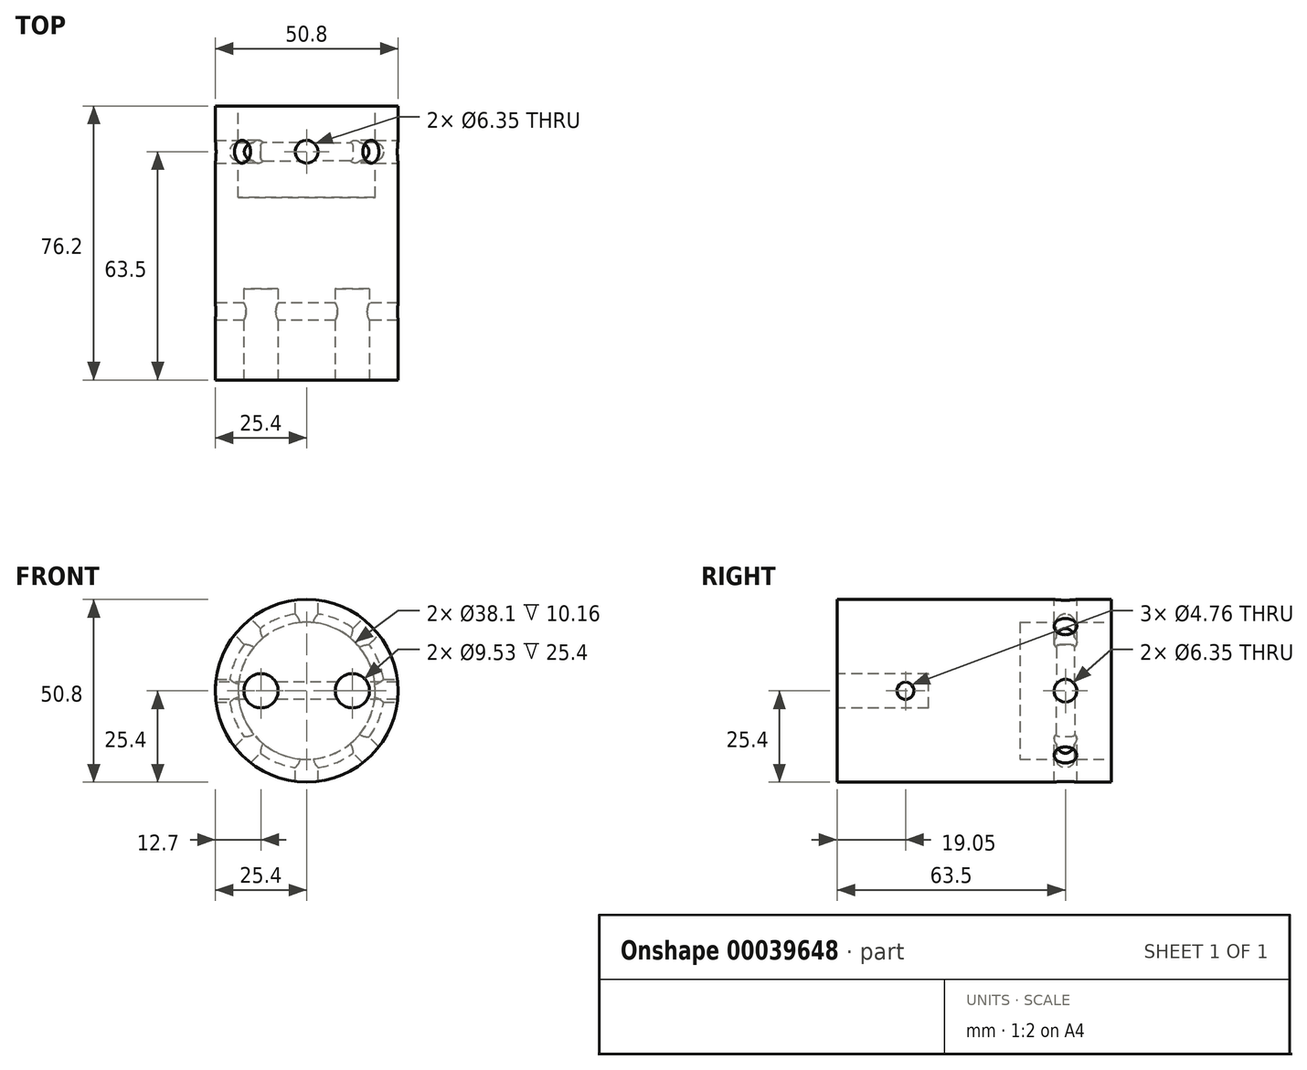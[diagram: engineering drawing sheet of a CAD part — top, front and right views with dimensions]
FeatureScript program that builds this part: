
annotation { "Feature Type Name" : "Feature", "Feature Type Description" : "" }
export const myFeature = defineFeature(function(context is Context, id is Id, definition is map)
    precondition{}
    {
        {
            var Q0;
            Q0=qCreatedBy(makeId("Top.planeOp"),FACE);
            var sketch = newSketch(context, id + "F0", { "sketchPlane" : qUnion([Q0])});
            skLineSegment(sketch, "E0", {"start": v(0, 0) * mm, "end": v(-19.05, 0) * mm});
            skLineSegment(sketch, "E1", {"start": v(0, 0) * mm, "end": v(19.05, 0) * mm});
            skLineSegment(sketch, "E2", {"start": v(19.05, 0) * mm, "end": v(25.4, 0) * mm});
            skLineSegment(sketch, "E3", {"start": v(25.4, 0) * mm, "end": v(25.4, -50.8) * mm});
            skLineSegment(sketch, "E4", {"start": v(25.4, -50.8) * mm, "end": v(-25.4, -50.8) * mm});
            skLineSegment(sketch, "E5", {"start": v(-25.4, -50.8) * mm, "end": v(-25.4, 0) * mm});
            skLineSegment(sketch, "E6", {"start": v(-25.4, 0) * mm, "end": v(-19.05, 0) * mm});
            skSolve(sketch);
        }
        {
            var Q0;
            Q0=makeQuery(id+"F0.imprint","IMPRINT",FACE,{"disambiguationData":[TD([[makeQuery(id+"F0.imprint","IMPRINT",EDGE,{"derivedFrom":sQuery(id+"F0.wireOp",EDGE,"7bc87d7a-c47a-405d-8f71-89237edce016")}),1.0]])]});
            var Q1;
            Q1=makeQuery(id+"F0.imprint","IMPRINT",FACE,{"disambiguationData":[TD([[makeQuery(id+"F0.imprint","IMPRINT",EDGE,{"derivedFrom":sQuery(id+"F0.wireOp",EDGE,"e6d046b3-f900-488c-85fe-59f8af33b7d6")}),-1.0]])]});
            var Q2;
            Q2=makeQuery(id+"F0.imprint","IMPRINT",FACE,{"disambiguationData":[TD([[makeQuery(id+"F0.imprint","IMPRINT",EDGE,{"derivedFrom":sQuery(id+"F0.wireOp",EDGE,"2ad4768f-a0cb-4b3a-8505-408e7b1cef2d")}),1.0]])]});
            var Q3;
            Q3=makeQuery(id+"F0.imprint","IMPRINT",FACE,{"disambiguationData":[TD([[makeQuery(id+"F0.imprint","IMPRINT",EDGE,{"derivedFrom":sQuery(id+"F0.wireOp",EDGE,"0ca17347-032e-40ac-bc44-827958d3e6fc")}),1.0]])]});
            var Q4;
            Q4=makeQuery(id+"F0.imprint","IMPRINT",FACE,{"disambiguationData":[TD([[makeQuery(id+"F0.imprint","IMPRINT",EDGE,{"derivedFrom":sQuery(id+"F0.wireOp",EDGE,"E0")}),1.0]])]});
            var Q5;
            Q5=makeQuery(id+"F0.imprint","IMPRINT",FACE,{"disambiguationData":[TD([[makeQuery(id+"F0.imprint","IMPRINT",EDGE,{"derivedFrom":sQuery(id+"F0.wireOp",EDGE,"4362853a-bfab-4841-ad33-0da4945ce7d8")}),-1.0]])]});
            var Q6;
            Q6=makeQuery(id+"F0.imprint","IMPRINT",FACE,{"disambiguationData":[TD([[makeQuery(id+"F0.imprint","IMPRINT",EDGE,{"derivedFrom":sQuery(id+"F0.wireOp",EDGE,"9ec19a48-1b8f-4e76-9588-66d74d53f144")}),-1.0]])]});
            var Q7;
            Q7=makeQuery(id+"F0.imprint","IMPRINT",FACE,{"disambiguationData":[TD([[makeQuery(id+"F0.imprint","IMPRINT",EDGE,{"derivedFrom":sQuery(id+"F0.wireOp",EDGE,"8e5a53d8-bfa6-4702-8b6f-d0fae9ec5a2a")}),1.0]])]});
            var Q8;
            Q8=makeQuery(id+"F0.imprint","IMPRINT",FACE,{"disambiguationData":[TD([[makeQuery(id+"F0.imprint","IMPRINT",EDGE,{"derivedFrom":sQuery(id+"F0.wireOp",EDGE,"134bd195-3179-4c87-b82c-456532974db7")}),1.0]])]});
            var Q9;
            Q9=makeQuery(id+"F0.imprint","IMPRINT",FACE,{"disambiguationData":[TD([[makeQuery(id+"F0.imprint","IMPRINT",EDGE,{"derivedFrom":sQuery(id+"F0.wireOp",EDGE,"030bf412-2708-412a-a3c6-39b4ca16a0eb")}),1.0]])]});
            var Q10;
            Q10=makeQuery(id+"F0.imprint","IMPRINT",FACE,{"disambiguationData":[TD([[makeQuery(id+"F0.imprint","IMPRINT",EDGE,{"derivedFrom":sQuery(id+"F0.wireOp",EDGE,"134bd195-3179-4c87-b82c-456532974db7")}),-1.0]])]});
            var Q11;
            Q11=makeQuery(id+"F0.imprint","IMPRINT",FACE,{"disambiguationData":[TD([[makeQuery(id+"F0.imprint","IMPRINT",EDGE,{"derivedFrom":sQuery(id+"F0.wireOp",EDGE,"5d857f63-e05d-4024-b1ce-ebe2b5560337")}),-1.0]])]});
            var Q12;
            Q12=makeQuery(id+"F0.imprint","IMPRINT",FACE,{"disambiguationData":[TD([[makeQuery(id+"F0.imprint","IMPRINT",EDGE,{"derivedFrom":sQuery(id+"F0.wireOp",EDGE,"e989e8fa-5b56-48d0-8351-93b8a3e71791")}),-1.0]])]});
            extrude(context, id + "F1", {"entities" : qUnion([Q0, Q1, Q2, Q3, Q4, Q5, Q6, Q7, Q8, Q9, Q10, Q11, Q12]), "endBound" : BoundingType.SYMMETRIC, "depth" : 50.8 * mm});
        }
        {
            var Q0;
            Q0=makeQuery(id+"F1.opExtrude","CAP_EDGE",EDGE,{"disambiguationData":[OSD([sQuery(id+"F0.wireOp",EDGE,"4362853a-bfab-4841-ad33-0da4945ce7d8")])],"isStart":false});
            var Q1;
            Q1=makeQuery(id+"F1.opExtrude","CAP_EDGE",EDGE,{"disambiguationData":[OSD([sQuery(id+"F0.wireOp",EDGE,"4362853a-bfab-4841-ad33-0da4945ce7d8")])],"isStart":true});
            var Q2;
            Q2=makeQuery(id+"F1.opExtrude","CAP_EDGE",EDGE,{"disambiguationData":[OSD([sQuery(id+"F0.wireOp",EDGE,"9ec19a48-1b8f-4e76-9588-66d74d53f144")])],"isStart":false});
            var Q3;
            Q3=makeQuery(id+"F1.opExtrude","CAP_EDGE",EDGE,{"disambiguationData":[OSD([sQuery(id+"F0.wireOp",EDGE,"9ec19a48-1b8f-4e76-9588-66d74d53f144")])],"isStart":true});
            var Q4;
            Q4=makeQuery(id+"F1.opExtrude","CAP_EDGE",EDGE,{"disambiguationData":[OSD([sQuery(id+"F0.wireOp",EDGE,"E5")])],"isStart":true});
            var Q5;
            Q5=makeQuery(id+"F1.opExtrude","CAP_EDGE",EDGE,{"disambiguationData":[OSD([sQuery(id+"F0.wireOp",EDGE,"E3")])],"isStart":true});
            var Q6;
            Q6=makeQuery(id+"F1.opExtrude","CAP_EDGE",EDGE,{"disambiguationData":[OSD([sQuery(id+"F0.wireOp",EDGE,"E5")])],"isStart":false});
            var Q7;
            Q7=makeQuery(id+"F1.opExtrude","CAP_EDGE",EDGE,{"disambiguationData":[OSD([sQuery(id+"F0.wireOp",EDGE,"E3")])],"isStart":false});
            fillet(context, id + "F2", {"entities" : qUnion([Q0, Q1, Q2, Q3, Q4, Q5, Q6, Q7]), "radius" : 25.4 * mm, "tangentPropagation" : true, "allowEdgeOverflow" : false});
        }
        {
            var Q0;
            Q0=makeQuery(id+"F1.opExtrude","SWEPT_FACE",FACE,{"disambiguationData":[OSD([sQuery(id+"F0.wireOp",EDGE,"E4")])]});
            extrude(context, id + "F3", {"entities" : qUnion([Q0]), "operationType" : NewBodyOperationType.ADD, "depth" : 25.4 * mm});
        }
        {
            var Q0;
            Q0=makeQuery(id+"F3.opExtrude","CAP_FACE",FACE,{"disambiguationData":[OSD([sQuery(id+"F0.wireOp",EDGE,"E4")])],"isStart":false});
            var sketch = newSketch(context, id + "F4", { "sketchPlane" : qUnion([Q0])});
            skLineSegment(sketch, "E7", {"start": v(0, -25.4) * mm, "end": v(0, 25.4) * mm});
            skArc(sketch, "E8", {"start": v(0, 25.4) * mm, "mid": v(-24.57, 0) * mm, "end": v(0, -25.4) * mm});
            skSolve(sketch);
        }
        {
            var Q0;
            {var subQ1=sQuery(id+"F4.wireOp",EDGE,"E7");Q0=makeQuery(id+"F4.imprint","IMPRINT",FACE,{"disambiguationData":[TD([[makeQuery(id+"F4.imprint","IMPRINT",EDGE,{"derivedFrom":subQ1}),-1.0]])]});}
            var sketch = newSketch(context, id + "F5", { "sketchPlane" : qUnion([Q0])});
            skLineSegment(sketch, "E9", {"start": v(0, 0) * mm, "end": v(12.7, 0) * mm});
            skLineSegment(sketch, "E10", {"start": v(0, 0) * mm, "end": v(-12.7, 0) * mm});
            skCircle(sketch, "E11", {"center": v(12.7, 0) * mm, "radius": 4.76 * mm});
            skCircle(sketch, "E12", {"center": v(-12.7, 0) * mm, "radius": 4.76 * mm});
            skSolve(sketch);
        }
        {
            var Q0;
            Q0=makeQuery(id+"F5.imprint","IMPRINT",FACE,{"disambiguationData":[TD([[makeQuery(id+"F5.imprint","IMPRINT",EDGE,{"derivedFrom":sQuery(id+"F5.wireOp",EDGE,"E12")}),1.0]])]});
            var Q1;
            Q1=makeQuery(id+"F5.imprint","IMPRINT",FACE,{"disambiguationData":[TD([[makeQuery(id+"F5.imprint","IMPRINT",EDGE,{"derivedFrom":sQuery(id+"F5.wireOp",EDGE,"E11")}),1.0]])]});
            extrude(context, id + "F6", {"entities" : qUnion([Q0, Q1]), "operationType" : NewBodyOperationType.REMOVE, "oppositeDirection" : true, "depth" : 25.4 * mm});
        }
        {
            var Q0;
            Q0=qCreatedBy(makeId("Right.planeOp"),FACE);
            var sketch = newSketch(context, id + "F7", { "sketchPlane" : qUnion([Q0])});
            skCircle(sketch, "E13", {"center": v(-57.15, 0) * mm, "radius": 2.38 * mm});
            skLineSegment(sketch, "E14.0", {"start": v(-76.2, -25.4) * mm, "end": v(-76.2, 25.4) * mm});
            skSolve(sketch);
        }
        {
            var Q0;
            Q0=makeQuery(id+"F1.opExtrude","SWEPT_FACE",FACE,{"disambiguationData":[OSD([sQuery(id+"F0.wireOp",EDGE,"E0"),sQuery(id+"F0.wireOp",EDGE,"E1"),sQuery(id+"F0.wireOp",EDGE,"E2"),sQuery(id+"F0.wireOp",EDGE,"E6")])]});
            var sketch = newSketch(context, id + "F8", { "sketchPlane" : qUnion([Q0])});
            skCircle(sketch, "E15", {"center": v(0, 0) * mm, "radius": 19.05 * mm});
            skSolve(sketch);
        }
        {
            var Q0;
            Q0 = qSketchRegion(id + "F8", true);
            extrude(context, id + "F9", {"entities" : qUnion([Q0]), "operationType" : NewBodyOperationType.REMOVE, "oppositeDirection" : true, "depth" : 25.4 * mm});
        }
        {
            var Q0;
            Q0 = qSketchRegion(id + "F7", true);
            extrude(context, id + "F10", {"entities" : qUnion([Q0]), "operationType" : NewBodyOperationType.REMOVE, "depth" : 127 * mm, "hasSecondDirection" : true, "secondDirectionOppositeDirection" : true, "secondDirectionDepth" : 127 * mm});
        }
        {
            var Q0;
            Q0=qCreatedBy(makeId("Right.planeOp"),FACE);
            var sketch = newSketch(context, id + "F11", { "sketchPlane" : qUnion([Q0])});
            skCircle(sketch, "E16", {"center": v(-12.7, 0) * mm, "radius": 3.18 * mm});
            skSolve(sketch);
        }
        {
            var Q0;
            Q0 = qSketchRegion(id + "F11", true);
            extrude(context, id + "F12", {"entities" : qUnion([Q0]), "operationType" : NewBodyOperationType.REMOVE, "oppositeDirection" : true, "depth" : 25.4 * mm, "hasSecondDirection" : true, "secondDirectionOppositeDirection" : false, "secondDirectionDepth" : 25.4 * mm});
        }
        {
            var Q0;
            Q0=qCreatedBy(makeId("Top.planeOp"),FACE);
            var sketch = newSketch(context, id + "F13", { "sketchPlane" : qUnion([Q0])});
            skCircle(sketch, "E17", {"center": v(0, -12.7) * mm, "radius": 3.18 * mm});
            skSolve(sketch);
        }
        {
            var Q0;
            Q0 = qSketchRegion(id + "F13", true);
            extrude(context, id + "F14", {"entities" : qUnion([Q0]), "operationType" : NewBodyOperationType.REMOVE, "oppositeDirection" : true, "depth" : 25.4 * mm, "hasSecondDirection" : true, "secondDirectionOppositeDirection" : false, "secondDirectionDepth" : 25.4 * mm});
        }
        {
            var Q0;
            Q0=qCreatedBy(makeId("Top.planeOp"),FACE);
            var sketch = newSketch(context, id + "F15", { "sketchPlane" : qUnion([Q0])});
            skCircle(sketch, "E18", {"center": v(-19.05, -12.7) * mm, "radius": 2.54 * mm});
            skSolve(sketch);
        }
        {
            var Q0;
            Q0=qCreatedBy(makeId("Top.planeOp"),FACE);
            var sketch = newSketch(context, id + "F16", { "sketchPlane" : qUnion([Q0])});
            skLineSegment(sketch, "E19", {"start": v(0, 0) * mm, "end": v(0, -26.9) * mm});
            skSolve(sketch);
        }
        {
            var Q0;
            Q0 = qSketchRegion(id + "F15", true);
            var Q1;
            Q1=sQuery(id+"F16.wireOp",EDGE,"E19");
            revolve(context, id + "F17", {"operationType" : NewBodyOperationType.REMOVE, "entities" : qUnion([Q0]), "axis" : qUnion([Q1]), "revolveType" : RevolveType.FULL});
        }
        {
            var Q0;
            Q0=makeQuery(id+"F12.boolean.opBoolean","COPY",FACE,{"disambiguationData":[OD(1.0)],"derivedFrom":makeQuery(id+"F12.opExtrude","SWEPT_FACE",FACE,{"disambiguationData":[OSD([sQuery(id+"F11.wireOp",EDGE,"E16")])]})});
            var Q1;
            Q1=makeQuery(id+"F14.boolean.opBoolean","COPY",FACE,{"disambiguationData":[OD(1.0)],"derivedFrom":makeQuery(id+"F14.opExtrude","SWEPT_FACE",FACE,{"disambiguationData":[OSD([sQuery(id+"F13.wireOp",EDGE,"E17")])]})});
            var Q2;
            Q2=makeQuery(id+"F12.boolean.opBoolean","COPY",FACE,{"disambiguationData":[OD(0.0)],"derivedFrom":makeQuery(id+"F12.opExtrude","SWEPT_FACE",FACE,{"disambiguationData":[OSD([sQuery(id+"F11.wireOp",EDGE,"E16")])]})});
            var Q3;
            Q3=makeQuery(id+"F14.boolean.opBoolean","COPY",FACE,{"disambiguationData":[OD(0.0)],"derivedFrom":makeQuery(id+"F14.opExtrude","SWEPT_FACE",FACE,{"disambiguationData":[OSD([sQuery(id+"F13.wireOp",EDGE,"E17")])]})});
            var Q4;
            Q4=sQuery(id+"F16.wireOp",EDGE,"E19");
            circularPattern(context, id + "F18", {"patternType" : PatternType.FACE, "faces" : qUnion([Q0, Q1, Q2, Q3]), "axis" : qUnion([Q4]), "angle" : 45 * degree, "instanceCount" : 2, "equalSpace" : true});
        }
    });
